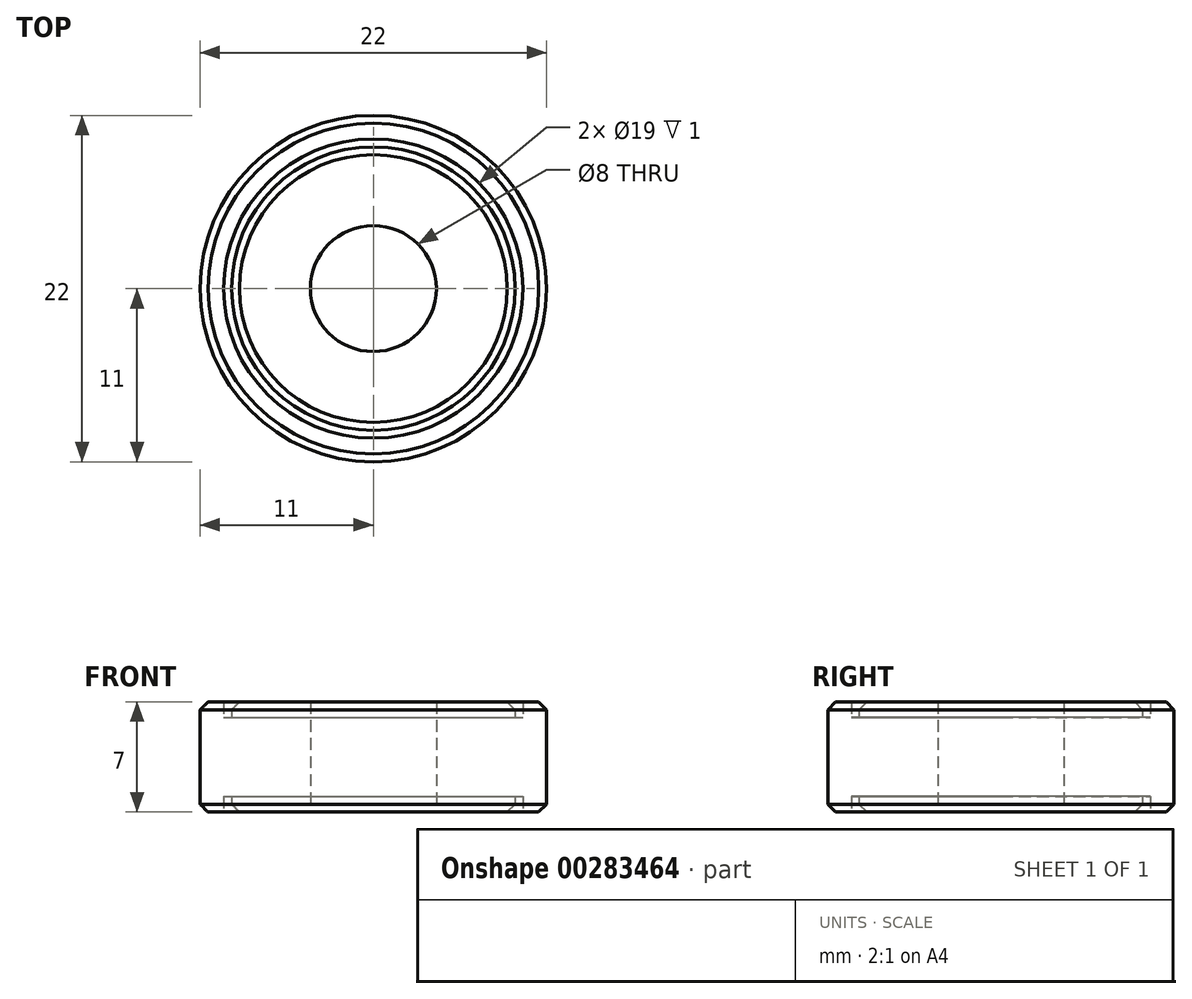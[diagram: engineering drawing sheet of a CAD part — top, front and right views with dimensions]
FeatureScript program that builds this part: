
annotation { "Feature Type Name" : "Feature", "Feature Type Description" : "" }
export const myFeature = defineFeature(function(context is Context, id is Id, definition is map)
    precondition{}
    {
        {
            var Q0;
            Q0=qCreatedBy(makeId("Front.planeOp"),FACE);
            var sketch = newSketch(context, id + "F0", { "sketchPlane" : qUnion([Q0])});
            skLineSegment(sketch, "E0", {"start": v(0, 2.89) * mm, "end": v(0, -5.57) * mm, "construction": true});
            skLineSegment(sketch, "E1", {"start": v(-4, 0) * mm, "end": v(-4, 3.5) * mm});
            skLineSegment(sketch, "E2", {"start": v(-4, 3.5) * mm, "end": v(-8.5, 3.5) * mm});
            skLineSegment(sketch, "E3", {"start": v(-8.5, 3.5) * mm, "end": v(-9, 3) * mm});
            skLineSegment(sketch, "E4", {"start": v(-9, 3) * mm, "end": v(-9, 2.5) * mm});
            skLineSegment(sketch, "E5", {"start": v(-9, 2.5) * mm, "end": v(-9.5, 2.5) * mm});
            skLineSegment(sketch, "E6", {"start": v(-9.5, 2.5) * mm, "end": v(-9.5, 3.5) * mm});
            skLineSegment(sketch, "E7", {"start": v(-9.5, 3.5) * mm, "end": v(-10.5, 3.5) * mm});
            skLineSegment(sketch, "E8", {"start": v(-10.5, 3.5) * mm, "end": v(-11, 3) * mm});
            skLineSegment(sketch, "E9", {"start": v(-11, 3) * mm, "end": v(-11, 0) * mm});
            skLineSegment(sketch, "E10", {"start": v(-4, 0) * mm, "end": v(-11, 0) * mm, "construction": true});
            skLineSegment(sketch, "E11.MirrorCS", {"start": v(-9, -3) * mm, "end": v(-9, -2.5) * mm});
            skLineSegment(sketch, "E12.MirrorCS", {"start": v(-8.5, -3.5) * mm, "end": v(-9, -3) * mm});
            skLineSegment(sketch, "E13.MirrorCS", {"start": v(-9, -2.5) * mm, "end": v(-9.5, -2.5) * mm});
            skLineSegment(sketch, "E14.MirrorCS", {"start": v(0, -2.89) * mm, "end": v(0, 5.57) * mm, "construction": true});
            skLineSegment(sketch, "E15.MirrorCS", {"start": v(-11, -3) * mm, "end": v(-11, 0) * mm});
            skLineSegment(sketch, "E16.MirrorCS", {"start": v(-4, -3.5) * mm, "end": v(-8.5, -3.5) * mm});
            skLineSegment(sketch, "E17.MirrorCS", {"start": v(-10.5, -3.5) * mm, "end": v(-11, -3) * mm});
            skLineSegment(sketch, "E18.MirrorCS", {"start": v(-9.5, -3.5) * mm, "end": v(-10.5, -3.5) * mm});
            skLineSegment(sketch, "E19.MirrorCS", {"start": v(-4, 0) * mm, "end": v(-4, -3.5) * mm});
            skLineSegment(sketch, "E20.MirrorCS", {"start": v(-9.5, -2.5) * mm, "end": v(-9.5, -3.5) * mm});
            skSolve(sketch);
        }
        {
            var Q0;
            Q0 = qSketchRegion(id + "F0", true);
            var Q1;
            Q1=sQuery(id+"F0.wireOp",EDGE,"E14.MirrorCS");
            revolve(context, id + "F1", {"entities" : qUnion([Q0]), "axis" : qUnion([Q1]), "revolveType" : RevolveType.FULL});
        }
    });
